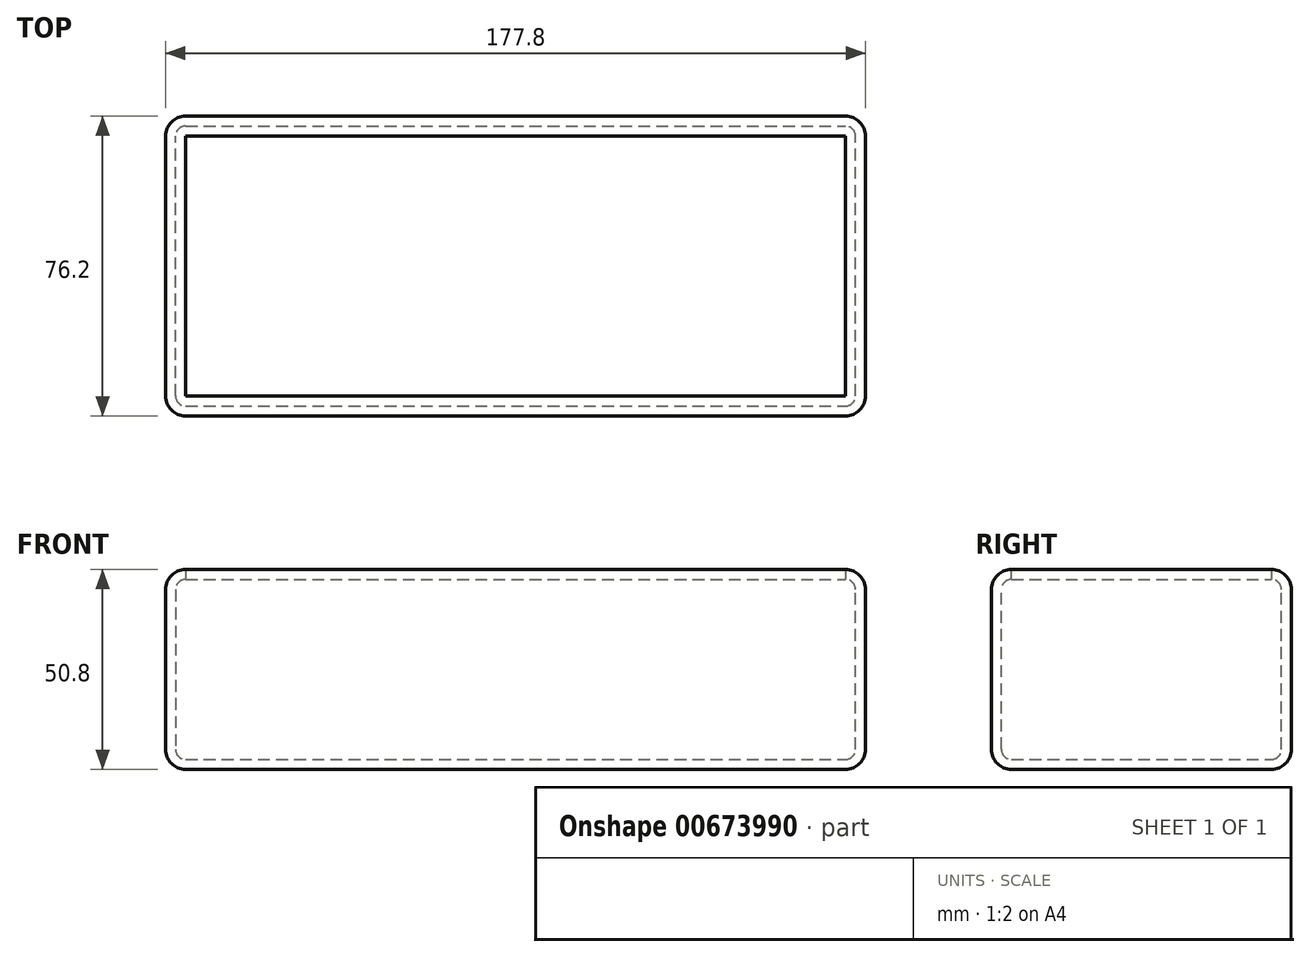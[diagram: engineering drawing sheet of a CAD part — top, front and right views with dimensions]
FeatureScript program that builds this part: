
annotation { "Feature Type Name" : "Feature", "Feature Type Description" : "" }
export const myFeature = defineFeature(function(context is Context, id is Id, definition is map)
    precondition{}
    {
        {
            var Q0;
            Q0=qCreatedBy(makeId("Front.planeOp"),FACE);
            var sketch = newSketch(context, id + "F0", { "sketchPlane" : qUnion([Q0])});
            skLineSegment(sketch, "E0", {"start": v(0, 0) * mm, "end": v(177.8, 0) * mm});
            skLineSegment(sketch, "E1", {"start": v(177.8, 0) * mm, "end": v(177.8, 50.8) * mm});
            skLineSegment(sketch, "E2", {"start": v(177.8, 50.8) * mm, "end": v(0, 50.8) * mm});
            skLineSegment(sketch, "E3", {"start": v(0, 50.8) * mm, "end": v(0, 0) * mm});
            skSolve(sketch);
        }
        {
            var Q0;
            Q0 = qSketchRegion(id + "F0", true);
            extrude(context, id + "F1", {"entities" : qUnion([Q0]), "depth" : 76.2 * mm, "offsetDistance" : 25.4 * mm});
        }
        {
            var Q0;
            Q0=makeQuery(id+"F1.opExtrude","CAP_EDGE",EDGE,{"disambiguationData":[OSD([sQuery(id+"F0.wireOp",EDGE,"E2")])],"isStart":false});
            var Q1;
            Q1=makeQuery(id+"F1.opExtrude","SWEPT_EDGE",EDGE,{"disambiguationData":[OSD([sQuery(id+"F0.wireOp",EDGE,"E1"),sQuery(id+"F0.wireOp",EDGE,"E2")])]});
            var Q2;
            Q2=makeQuery(id+"F1.opExtrude","CAP_EDGE",EDGE,{"disambiguationData":[OSD([sQuery(id+"F0.wireOp",EDGE,"E1")])],"isStart":false});
            var Q3;
            Q3=makeQuery(id+"F1.opExtrude","CAP_EDGE",EDGE,{"disambiguationData":[OSD([sQuery(id+"F0.wireOp",EDGE,"E0")])],"isStart":false});
            var Q4;
            Q4=makeQuery(id+"F1.opExtrude","SWEPT_FACE",FACE,{"disambiguationData":[OSD([sQuery(id+"F0.wireOp",EDGE,"E1")])]});
            var Q5;
            Q5=makeQuery(id+"F1.opExtrude","CAP_EDGE",EDGE,{"disambiguationData":[OSD([sQuery(id+"F0.wireOp",EDGE,"E2")])],"isStart":true});
            var Q6;
            Q6=makeQuery(id+"F1.opExtrude","CAP_FACE",FACE,{"disambiguationData":[OSD([sQuery(id+"F0.wireOp",EDGE,"E0"),sQuery(id+"F0.wireOp",EDGE,"E1"),sQuery(id+"F0.wireOp",EDGE,"E2"),sQuery(id+"F0.wireOp",EDGE,"E3")])],"isStart":true});
            var Q7;
            Q7=makeQuery(id+"F1.opExtrude","SWEPT_EDGE",EDGE,{"disambiguationData":[OSD([sQuery(id+"F0.wireOp",EDGE,"E2"),sQuery(id+"F0.wireOp",EDGE,"E3")])]});
            var Q8;
            Q8=makeQuery(id+"F1.opExtrude","SWEPT_EDGE",EDGE,{"disambiguationData":[OSD([sQuery(id+"F0.wireOp",EDGE,"E0"),sQuery(id+"F0.wireOp",EDGE,"E3")])]});
            var Q9;
            Q9=makeQuery(id+"F1.opExtrude","CAP_EDGE",EDGE,{"disambiguationData":[OSD([sQuery(id+"F0.wireOp",EDGE,"E3")])],"isStart":false});
            var Q10;
            Q10=makeQuery(id+"F1.opExtrude","CAP_EDGE",EDGE,{"disambiguationData":[OSD([sQuery(id+"F0.wireOp",EDGE,"E3")])],"isStart":true});
            fillet(context, id + "F2", {"entities" : qUnion([Q0, Q1, Q2, Q3, Q4, Q5, Q6, Q7, Q8, Q9, Q10]), "radius" : 5.08 * mm, "tangentPropagation" : true, "allowEdgeOverflow" : false});
        }
        {
            var Q0;
            Q0=makeQuery(id+"F1.opExtrude","SWEPT_FACE",FACE,{"disambiguationData":[OSD([sQuery(id+"F0.wireOp",EDGE,"E2")])]});
            shell(context, id + "F3", {"entities" : qUnion([Q0]), "thickness" : 2.54 * mm});
        }
    });
